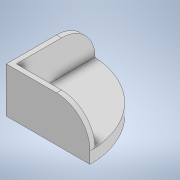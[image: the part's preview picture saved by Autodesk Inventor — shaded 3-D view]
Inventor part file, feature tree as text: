
AUTODESK INVENTOR PART (.ipt)
format: ipt  version: 2020 (Build 240168000, 168)  size: 143,360 bytes
history: native  units: mm
features: sketch x5, extrude x4, fillet x2, hole x1
ambient origin geometry x8: Origin, YZ Plane, XZ Plane, XY Plane, X Axis, Y Axis, Z Axis, Center Point
bodies: Solid1 (feature_tree)
feature tree (12):
  extrude  "Extrusion1"  Depth=7.0mm TaperAngle=0.0deg
  extrude  "Extrusion2"  Depth=3.0mm
  extrude  "Extrusion3"  Depth=3.0mm
  extrude  "Extrusion4"  Depth=20.0mm TaperAngle=0.0deg
  hole  "Hole1"  [1 undecoded]
  fillet  "Fillet1"  Radius=50.0mm
  fillet  "Fillet2"  Radius=50.0mm
  sketch  "Sketch1"  dims[d0=100.0mm d1=7.0mm d2=0.0mm]
  sketch  "Sketch2"  dims[d3=50.0mm d4=3.0mm]
  sketch  "Sketch3"  dims[d5=20.0mm d6=0.0mm d7=3.0mm]
  sketch  "Sketch4"  dims[d8=50.0mm d9=20.0mm d10=0.0mm]
  sketch  "Sketch5"  dims[d11=50.0mm d12=100.0mm d13=50.0mm d14=50.0mm d15=7.0mm d16=0.0mm d17=6.5mm d18=6.0mm d19=10.5mm d20=5.0mm d21=90.0deg d22=8.0mm d23=20.594885mm d24=20.0mm d25=10.0mm d26=20.0mm d27=20.0mm]
note: 1 required parameter value undecoded (feature->parameter linkage not recoverable at this tier; creation-order binding heuristic only, values carry confidence <= 0.55)
